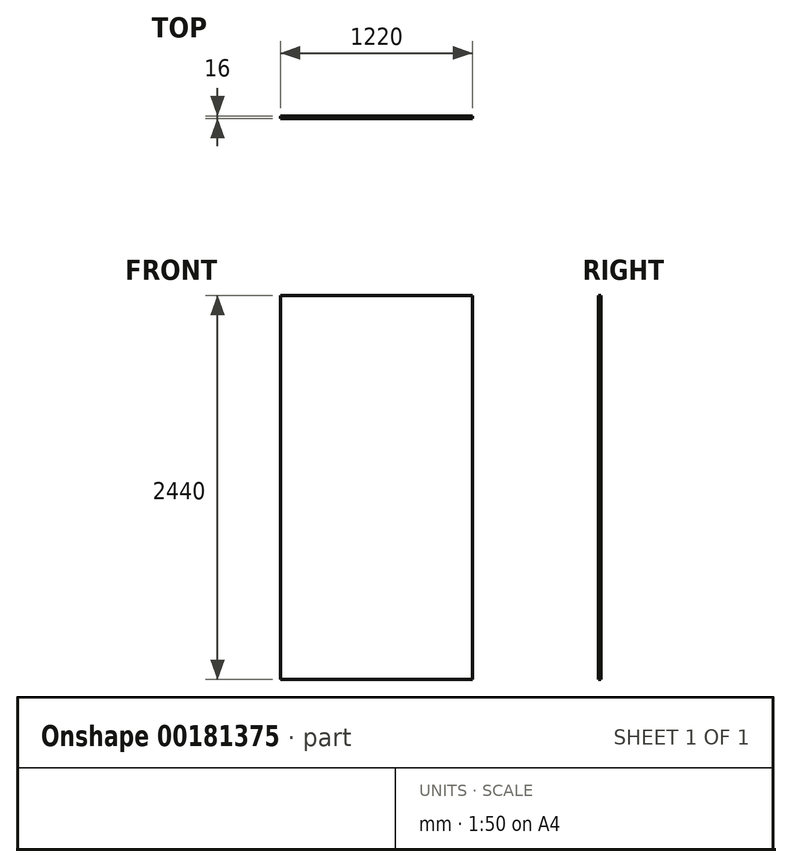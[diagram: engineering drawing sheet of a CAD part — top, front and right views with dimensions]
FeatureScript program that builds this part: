
annotation { "Feature Type Name" : "Feature", "Feature Type Description" : "" }
export const myFeature = defineFeature(function(context is Context, id is Id, definition is map)
    precondition{}
    {
        {
            var Q0;
            Q0=qCreatedBy(makeId("Front.planeOp"),FACE);
            var sketch = newSketch(context, id + "F0", { "sketchPlane" : qUnion([Q0])});
            skLineSegment(sketch, "E0.bottom", {"start": v(610, 1220) * mm, "end": v(-610, 1220) * mm});
            skLineSegment(sketch, "E0.top", {"start": v(610, -1220) * mm, "end": v(-610, -1220) * mm});
            skLineSegment(sketch, "E0.left", {"start": v(610, 1220) * mm, "end": v(610, -1220) * mm});
            skLineSegment(sketch, "E0.right", {"start": v(-610, 1220) * mm, "end": v(-610, -1220) * mm});
            skPoint(sketch, "E0.middle", {"position": v(0, 0) * mm});
            skSolve(sketch);
        }
        {
            var Q0;
            Q0 = qSketchRegion(id + "F0", true);
            extrude(context, id + "F1", {"entities" : qUnion([Q0]), "endBound" : BoundingType.SYMMETRIC, "depth" : 16 * mm});
        }
    });
